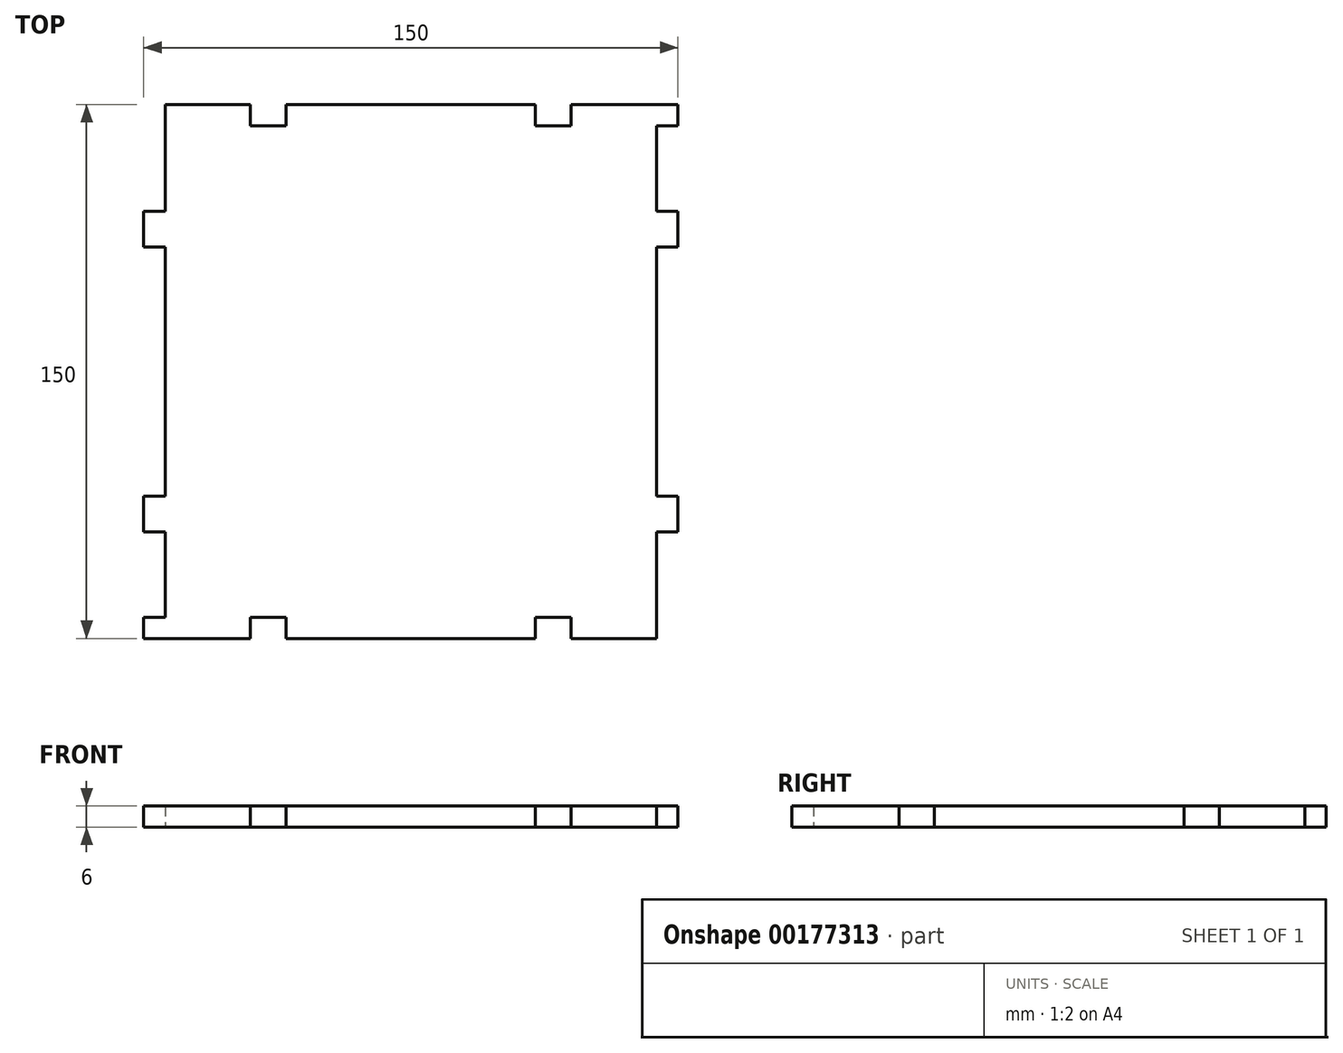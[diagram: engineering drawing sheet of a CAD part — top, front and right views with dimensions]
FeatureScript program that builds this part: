
annotation { "Feature Type Name" : "Feature", "Feature Type Description" : "" }
export const myFeature = defineFeature(function(context is Context, id is Id, definition is map)
    precondition{}
    {
        {
            var Q0;
            Q0=qCreatedBy(makeId("Top.planeOp"),FACE);
            var sketch = newSketch(context, id + "F0", { "sketchPlane" : qUnion([Q0])});
            skPoint(sketch, "E0.middle", {"position": v(0, 0) * mm});
            skLineSegment(sketch, "E1.bottom", {"start": v(69, -75) * mm, "end": v(-69, -75) * mm});
            skLineSegment(sketch, "E1.top", {"start": v(69, 75) * mm, "end": v(-69, 75) * mm});
            skLineSegment(sketch, "E1.left", {"start": v(69, -75) * mm, "end": v(69, 75) * mm});
            skLineSegment(sketch, "E1.right", {"start": v(-69, -75) * mm, "end": v(-69, 75) * mm});
            skLineSegment(sketch, "E2", {"start": v(-69, 75) * mm, "end": v(-45, 75) * mm, "construction": true});
            skLineSegment(sketch, "E3", {"start": v(-45, 75) * mm, "end": v(-45, 69) * mm});
            skLineSegment(sketch, "E4", {"start": v(-45, 69) * mm, "end": v(-35, 69) * mm});
            skLineSegment(sketch, "E5", {"start": v(-35, 69) * mm, "end": v(-35, 75) * mm});
            skLineSegment(sketch, "E6", {"start": v(0, 0) * mm, "end": v(-69, 0) * mm, "construction": true});
            skLineSegment(sketch, "E7", {"start": v(0, 0) * mm, "end": v(0, 75) * mm, "construction": true});
            skLineSegment(sketch, "E8.MirrorCS", {"start": v(45, 69) * mm, "end": v(35, 69) * mm});
            skLineSegment(sketch, "E9.MirrorCS", {"start": v(35, 69) * mm, "end": v(35, 75) * mm});
            skLineSegment(sketch, "E10.MirrorCS", {"start": v(45, 75) * mm, "end": v(45, 69) * mm});
            skLineSegment(sketch, "E11.MirrorCS", {"start": v(0, 0) * mm, "end": v(69, 0) * mm, "construction": true});
            skLineSegment(sketch, "E12.MirrorCS", {"start": v(-45, 63) * mm, "end": v(-45, 69) * mm});
            skLineSegment(sketch, "E13.MirrorCS", {"start": v(-45, -75) * mm, "end": v(-45, -69) * mm});
            skLineSegment(sketch, "E14.MirrorCS", {"start": v(-45, -69) * mm, "end": v(-35, -69) * mm});
            skLineSegment(sketch, "E15.MirrorCS", {"start": v(-35, -69) * mm, "end": v(-35, -75) * mm});
            skLineSegment(sketch, "E16.MirrorCS", {"start": v(35, -69) * mm, "end": v(35, -75) * mm});
            skLineSegment(sketch, "E17.MirrorCS", {"start": v(45, -69) * mm, "end": v(35, -69) * mm});
            skLineSegment(sketch, "E18.MirrorCS", {"start": v(45, -75) * mm, "end": v(45, -69) * mm});
            skLineSegment(sketch, "E19", {"start": v(-69, 75) * mm, "end": v(-69, 45) * mm});
            skLineSegment(sketch, "E20", {"start": v(-69, 45) * mm, "end": v(-75, 45) * mm});
            skLineSegment(sketch, "E21", {"start": v(-75, 45) * mm, "end": v(-75, 35) * mm});
            skLineSegment(sketch, "E22", {"start": v(-75, 35) * mm, "end": v(-69, 35) * mm});
            skLineSegment(sketch, "E23.MirrorCS", {"start": v(-75, -35) * mm, "end": v(-69, -35) * mm});
            skLineSegment(sketch, "E24.MirrorCS", {"start": v(-75, -45) * mm, "end": v(-75, -35) * mm});
            skLineSegment(sketch, "E25.MirrorCS", {"start": v(-69, -45) * mm, "end": v(-75, -45) * mm});
            skLineSegment(sketch, "E26.MirrorCS", {"start": v(69, 45) * mm, "end": v(75, 45) * mm});
            skLineSegment(sketch, "E27.MirrorCS", {"start": v(75, 45) * mm, "end": v(75, 35) * mm});
            skLineSegment(sketch, "E28.MirrorCS", {"start": v(75, 35) * mm, "end": v(69, 35) * mm});
            skLineSegment(sketch, "E29.MirrorCS", {"start": v(75, -35) * mm, "end": v(69, -35) * mm});
            skLineSegment(sketch, "E30.MirrorCS", {"start": v(75, -45) * mm, "end": v(75, -35) * mm});
            skLineSegment(sketch, "E31.MirrorCS", {"start": v(69, -45) * mm, "end": v(75, -45) * mm});
            skLineSegment(sketch, "E32", {"start": v(-69, -75) * mm, "end": v(-75, -75) * mm});
            skLineSegment(sketch, "E33", {"start": v(-75, -75) * mm, "end": v(-75, -69) * mm});
            skLineSegment(sketch, "E34", {"start": v(-75, -69) * mm, "end": v(-69, -69) * mm});
            skLineSegment(sketch, "E35.MirrorCS", {"start": v(-75, 75) * mm, "end": v(-75, 69) * mm});
            skLineSegment(sketch, "E36.MirrorCS", {"start": v(-69, 75) * mm, "end": v(-75, 75) * mm});
            skLineSegment(sketch, "E37.MirrorCS", {"start": v(-75, 69) * mm, "end": v(-69, 69) * mm});
            skLineSegment(sketch, "E38.MirrorCS", {"start": v(69, -75) * mm, "end": v(75, -75) * mm});
            skLineSegment(sketch, "E39.MirrorCS", {"start": v(75, -75) * mm, "end": v(75, -69) * mm});
            skLineSegment(sketch, "E40.MirrorCS", {"start": v(75, -69) * mm, "end": v(69, -69) * mm});
            skLineSegment(sketch, "E41.MirrorCS", {"start": v(69, 75) * mm, "end": v(75, 75) * mm});
            skLineSegment(sketch, "E42.MirrorCS", {"start": v(75, 75) * mm, "end": v(75, 69) * mm});
            skLineSegment(sketch, "E43.MirrorCS", {"start": v(75, 69) * mm, "end": v(69, 69) * mm});
            skSolve(sketch);
        }
        {
            var Q0;
            {var subQ0=sQuery(id+"F0.wireOp",EDGE,"E20");Q0=makeQuery(id+"F0.imprint","IMPRINT",FACE,{"disambiguationData":[TD([[makeQuery(id+"F0.imprint","IMPRINT",EDGE,{"derivedFrom":subQ0}),1.0]])]});}
            var Q1;
            {var subQ3=sQuery(id+"F0.wireOp",EDGE,"E3");Q1=makeQuery(id+"F0.imprint","IMPRINT",FACE,{"disambiguationData":[TD([[makeQuery(id+"F0.imprint","IMPRINT",EDGE,{"derivedFrom":subQ3}),-1.0]])]});}
            var Q2;
            {var subQ0=sQuery(id+"F0.wireOp",EDGE,"E23.MirrorCS");Q2=makeQuery(id+"F0.imprint","IMPRINT",FACE,{"disambiguationData":[TD([[makeQuery(id+"F0.imprint","IMPRINT",EDGE,{"derivedFrom":subQ0}),-1.0]])]});}
            var Q3;
            {var subQ0=sQuery(id+"F0.wireOp",EDGE,"E29.MirrorCS");Q3=makeQuery(id+"F0.imprint","IMPRINT",FACE,{"disambiguationData":[TD([[makeQuery(id+"F0.imprint","IMPRINT",EDGE,{"derivedFrom":subQ0}),1.0]])]});}
            var Q4;
            {var subQ0=sQuery(id+"F0.wireOp",EDGE,"E26.MirrorCS");Q4=makeQuery(id+"F0.imprint","IMPRINT",FACE,{"disambiguationData":[TD([[makeQuery(id+"F0.imprint","IMPRINT",EDGE,{"derivedFrom":subQ0}),-1.0]])]});}
            var Q5;
            {var subQ0=sQuery(id+"F0.wireOp",EDGE,"E32");Q5=makeQuery(id+"F0.imprint","IMPRINT",FACE,{"disambiguationData":[TD([[makeQuery(id+"F0.imprint","IMPRINT",EDGE,{"derivedFrom":subQ0}),-1.0]])]});}
            var Q6;
            {var subQ0=sQuery(id+"F0.wireOp",EDGE,"E41.MirrorCS");Q6=makeQuery(id+"F0.imprint","IMPRINT",FACE,{"disambiguationData":[TD([[makeQuery(id+"F0.imprint","IMPRINT",EDGE,{"derivedFrom":subQ0}),-1.0]])]});}
            extrude(context, id + "F1", {"entities" : qUnion([Q0, Q1, Q2, Q3, Q4, Q5, Q6]), "depth" : 6 * mm});
        }
    });
